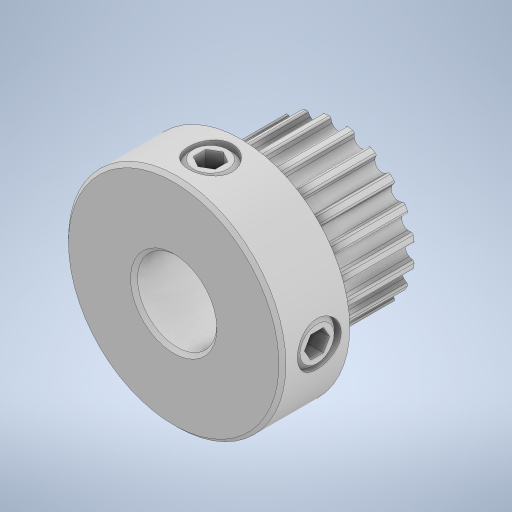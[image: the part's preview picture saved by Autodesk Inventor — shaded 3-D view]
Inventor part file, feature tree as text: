
AUTODESK INVENTOR PART (.ipt)
format: ipt  version: 2024 (Build 280153000, 153)  size: 454,144 bytes
history: native  units: in
note: dims shown in document units (in); Inventor stores cm internally (conversion verified against a paired STEP export)
features: extrude x1, sketch x1, projected_geometry x1, chamfer x1
ambient origin geometry x8: Origin, YZ Plane, XZ Plane, XY Plane, X Axis, Y Axis, Z Axis, Center Point
bodies: Solid1 (feature_tree)
feature tree (4):
  extrude  "Extrusion1"  [1 undecoded]
  sketch  "Sketch1"  dims[d0=0.0433in d1=0.0in]
  projected_geometry  "Projected Loop1"
  chamfer  "Chamfer1"  [1 undecoded]
note: 2 required parameter values undecoded (feature->parameter linkage not recoverable at this tier; creation-order binding heuristic only, values carry confidence <= 0.55)
